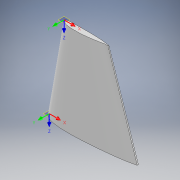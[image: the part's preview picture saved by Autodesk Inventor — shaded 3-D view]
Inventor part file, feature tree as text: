
AUTODESK INVENTOR PART (.ipt)
format: ipt  version: 2020 (Build 240168000, 168)  size: 267,264 bytes
history: native  units: mm
features: other x21, plane x2, loft x1
ambient origin geometry x8: Origin, YZ Plane, XZ Plane, XY Plane, X Axis, Y Axis, Z Axis, Center Point
bodies: Solid1 (feature_tree)
feature tree (24):
  other  "root_section"
  other  "tip_section"
  other  "planform"
  plane  "Work Plane8"
  plane  "Work Plane9"
  other  "root_plane_base"
  other  "tip_plane_base"
  other  "UCS_root"
  other  "UCS_tip"
  loft  "Loft1"
  other  "UCS_root: YZ Plane"
  other  "UCS_root: XZ Plane"
  other  "UCS_root: XY Plane"
  other  "UCS_root: X Axis"
  other  "UCS_root: Y Axis"
  other  "UCS_root: Z Axis"
  other  "UCS_root: Center Point"
  other  "UCS_tip: YZ Plane"
  other  "UCS_tip: XZ Plane"
  other  "UCS_tip: XY Plane"
  other  "UCS_tip: X Axis"
  other  "UCS_tip: Y Axis"
  other  "UCS_tip: Z Axis"
  other  "UCS_tip: Center Point"
